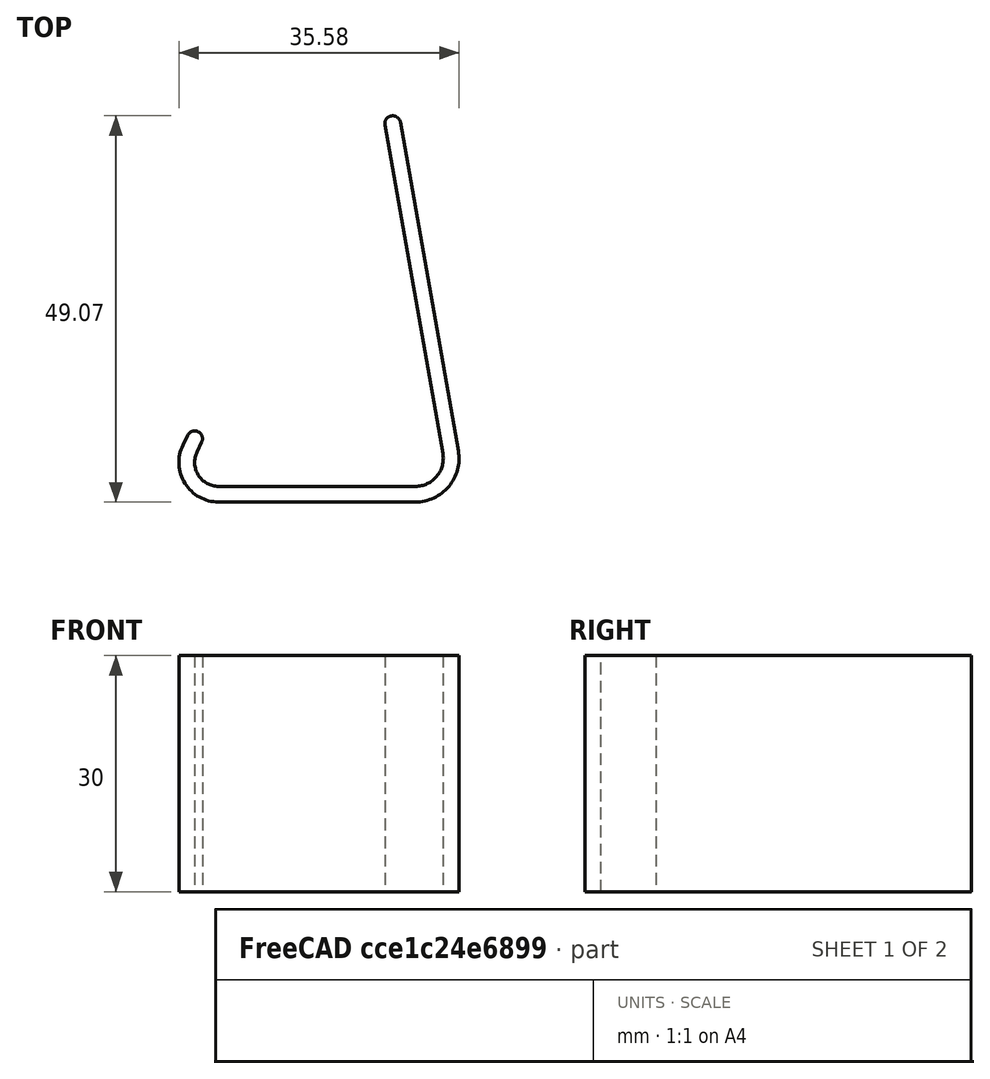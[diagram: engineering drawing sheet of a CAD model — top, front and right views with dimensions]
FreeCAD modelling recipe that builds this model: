
FCSTD DOCUMENT  (FreeCAD 0.20R27319 (Git))
Label: Plate stand single piece
License: All rights reserved
LicenseURL: http://en.wikipedia.org/wiki/All_rights_reserved
objects: Sketcher::SketchObject×1, PartDesign::Pad×1, PartDesign::Body×1
note: 4 computed .brp shape members not serialized (recipe doc carries the construction recipe); baked Part::Feature solids carry a one-line shape summary decoded from their .brp

FEATURE [Sketcher::SketchObject] Sketch
  FullyConstrained = false
  MapMode = 5
  Support = -> [XY_Plane]
  sketch-geometry (15):
    g0: LineSegment StartX=-3.58672 StartY=5.80299 StartZ=0 EndX=-3.81822 EndY=4.80095 EndZ=0
    g1: ArcOfCircle CenterX=0 CenterY=3.9188 CenterZ=0 NormalX=0 NormalY=0 NormalZ=1 AngleXU=0 Radius=3.9188 StartAngle=2.91454 EndAngle=4.71239
    g2: LineSegment StartX=-7e-16 StartY=0 StartZ=0 EndX=25 EndY=0 EndZ=0
    g3: ArcOfCircle CenterX=25 CenterY=3.56674 CenterZ=0 NormalX=0 NormalY=0 NormalZ=1 AngleXU=0 Radius=3.56674 StartAngle=4.71239 EndAngle=6.44909
    g4: LineSegment StartX=28.5178 StartY=4.15576 StartZ=0 EndX=21.0863 EndY=48.5379 EndZ=0
    g5: LineSegment StartX=-3.58672 StartY=5.80299 StartZ=0 EndX=-5.53538 EndY=6.2532 EndZ=0
    g6: LineSegment StartX=-5.53538 StartY=6.2532 StartZ=0 EndX=-5.76689 EndY=5.25116 EndZ=0
    g7: ArcOfCircle CenterX=0 CenterY=3.9188 CenterZ=0 NormalX=0 NormalY=0 NormalZ=1 AngleXU=0 Radius=5.9188 StartAngle=2.91454 EndAngle=4.71239
    g8: LineSegment StartX=0 StartY=-2 StartZ=0 EndX=25 EndY=-2 EndZ=0
    g9: ArcOfCircle CenterX=25 CenterY=3.56674 CenterZ=0 NormalX=0 NormalY=0 NormalZ=1 AngleXU=0 Radius=5.56674 StartAngle=4.71239 EndAngle=6.44909
    g10: LineSegment StartX=30.4903 StartY=4.48605 StartZ=0 EndX=23.0588 EndY=48.8682 EndZ=0
    g11: LineSegment StartX=23.0588 StartY=48.8682 StartZ=0 EndX=21.0863 EndY=48.5379 EndZ=0
    g12: ArcOfCircle CenterX=22.0726 CenterY=48.703 CenterZ=0 NormalX=0 NormalY=0 NormalZ=1 AngleXU=0 Radius=1 StartAngle=0.16591 EndAngle=3.3075
    g13: ArcOfCircle CenterX=-4.56105 CenterY=6.02809 CenterZ=0 NormalX=0 NormalY=0 NormalZ=1 AngleXU=0 Radius=1 StartAngle=6.05613 EndAngle=9.19773
    g14: LineSegment StartX=-3.58672 StartY=5.80299 StartZ=0 EndX=21.0863 EndY=48.5379 EndZ=0
  constraints (33):
    c: Tangent(g0,g1) = -1.5708
    c: PointOnObject(g2,g-1)
    c: Tangent(g2,g3) = -1.5708
    c: Tangent(g3,g4) = -1.5708
    c: Coincident(g0,g5)
    c: Coincident(g5,g6)
    c: Horizontal(g8)
    c: Tangent(g8,g9) = -1.5708
    c: Coincident(g10,g11)
    c: Coincident(g11,g4)
    c: Coincident(g3,g9)
    c: Coincident(g7,g1)
    c: Tangent(g1,g2) = -1.5708
    c: Tangent(g7,g8) = -1.5708
    c: Perpendicular(g0,g5)
    c: Parallel(g6,g0)
    c: Parallel(g4,g10)
    c: Equal(g5,g11)
    c: Distance(g11) = 2
    c: Tangent(g6,g7) = -1.5708
    c: Tangent(g9,g10) = -1.5708
    c: Distance(g8) = 25
    c: Coincident(g12,g4)
    c: Coincident(g12,g10)
    c: PointOnObject(g12,g11)
    c: Coincident(g13,g6)
    c: Coincident(g13,g0)
    c: PointOnObject(g13,g5)
    c: Coincident(g1,g-1)
    c: Coincident(g14,g0)
    c: Coincident(g14,g4)
    c: Angle(g2,g14) = 1.0472
    c: Distance(g10) = 45
FEATURE [PartDesign::Pad] Pad
  Direction = (0,0,1)
  Length = 30
  Length2 = 10
  Profile = -> Sketch
  ReferenceAxis = -> Sketch [N_Axis]
  Type = 0
FEATURE [PartDesign::Body] Body
  Group = -> [Sketch,Pad]
  Origin = -> Origin
  Tip = -> Pad
